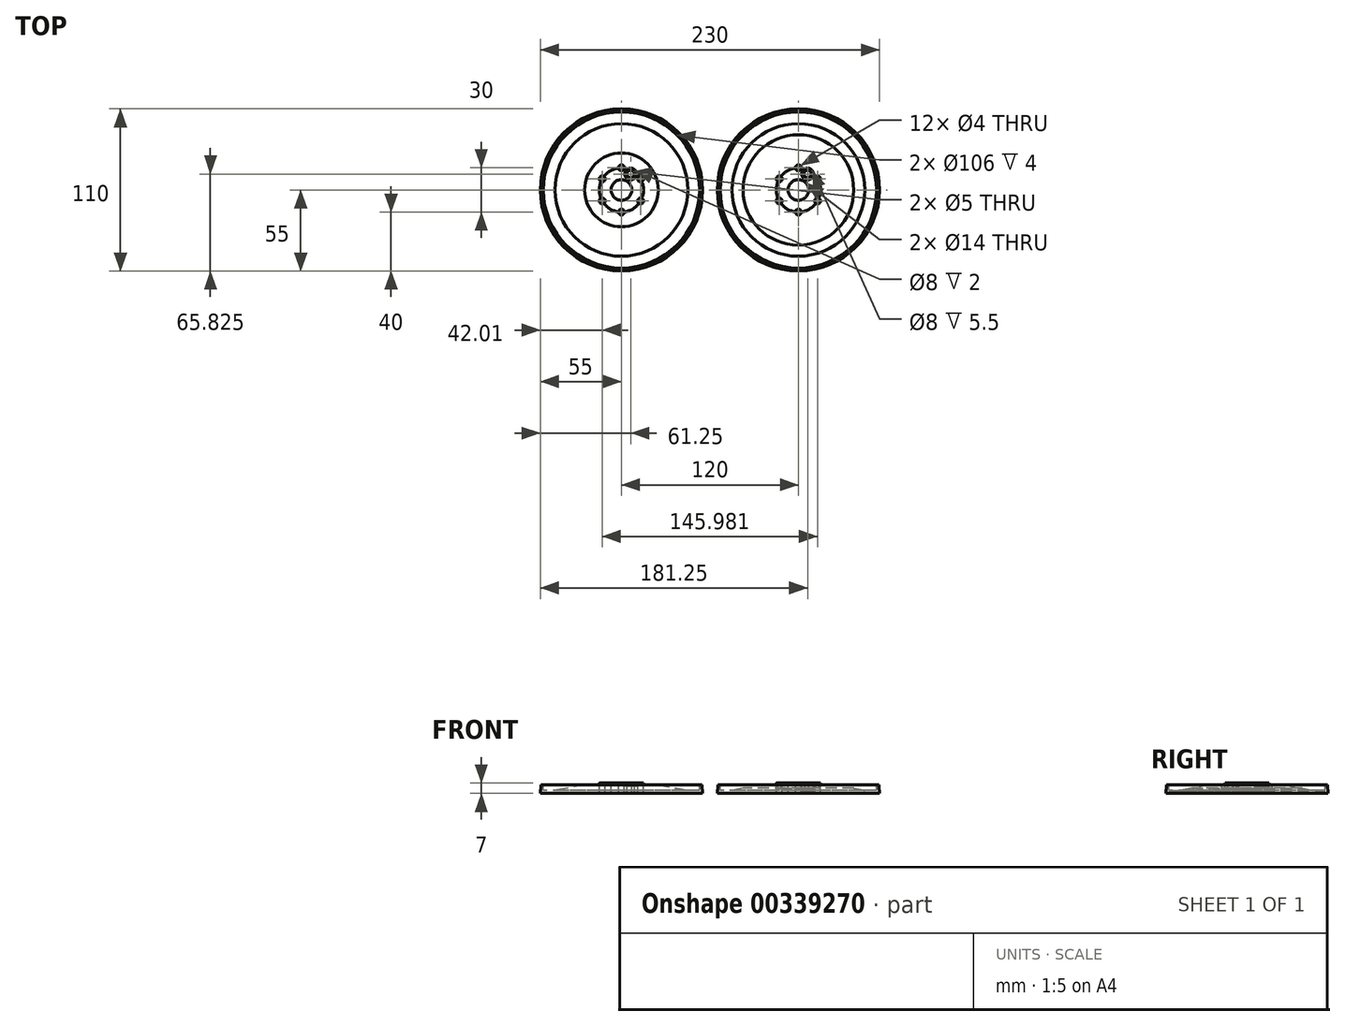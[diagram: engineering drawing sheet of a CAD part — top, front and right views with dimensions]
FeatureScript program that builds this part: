
annotation { "Feature Type Name" : "Feature", "Feature Type Description" : "" }
export const myFeature = defineFeature(function(context is Context, id is Id, definition is map)
    precondition{}
    {
        {
            var Q0;
            Q0=qCreatedBy(makeId("Front.planeOp"),FACE);
            var sketch = newSketch(context, id + "F0", { "sketchPlane" : qUnion([Q0])});
            skLineSegment(sketch, "E0", {"start": v(0, 0) * mm, "end": v(55, 0) * mm});
            skLineSegment(sketch, "E1", {"start": v(55, 0) * mm, "end": v(54.5, 6) * mm});
            skLineSegment(sketch, "E2", {"start": v(54.5, 6) * mm, "end": v(53, 6) * mm});
            skLineSegment(sketch, "E3", {"start": v(53, 6) * mm, "end": v(53, 2) * mm});
            skLineSegment(sketch, "E4", {"start": v(53, 2) * mm, "end": v(45, 2) * mm});
            skLineSegment(sketch, "E5", {"start": v(45, 2) * mm, "end": v(25, 6) * mm});
            skLineSegment(sketch, "E6", {"start": v(0, 7) * mm, "end": v(0, 0) * mm});
            skLineSegment(sketch, "E7", {"start": v(25, 6) * mm, "end": v(15, 6) * mm});
            skLineSegment(sketch, "E8", {"start": v(15, 6) * mm, "end": v(15, 7) * mm});
            skLineSegment(sketch, "E9", {"start": v(15, 7) * mm, "end": v(0, 7) * mm});
            skLineSegment(sketch, "E10", {"start": v(0, 25) * mm, "end": v(0, -25) * mm, "construction": true});
            skSolve(sketch);
        }
        {
            var Q0;
            Q0=makeQuery(id+"F0.imprint","IMPRINT",FACE,{"disambiguationData":[TD([[makeQuery(id+"F0.imprint","IMPRINT",EDGE,{"derivedFrom":sQuery(id+"F0.wireOp",EDGE,"E0")}),1.0]])]});
            var Q1;
            Q1=sQuery(id+"F0.wireOp",EDGE,"E10");
            revolve(context, id + "F1", {"entities" : qUnion([Q0]), "axis" : qUnion([Q1]), "revolveType" : RevolveType.FULL});
        }
        {
            var Q0;
            Q0=makeQuery(id+"F1.opRevolve","SWEPT_FACE",FACE,{"disambiguationData":[OSD([sQuery(id+"F0.wireOp",EDGE,"E9")])]});
            var sketch = newSketch(context, id + "F2", { "sketchPlane" : qUnion([Q0])});
            skCircle(sketch, "E11", {"center": v(0, 15) * mm, "radius": 2 * mm});
            skCircle(sketch, "E12", {"center": v(6.25, 10.83) * mm, "radius": 2.5 * mm});
            skCircle(sketch, "E13", {"center": v(6.25, 10.83) * mm, "radius": 4 * mm});
            skLineSegment(sketch, "E14", {"start": v(0, 15) * mm, "end": v(0, 0) * mm, "construction": true});
            skLineSegment(sketch, "E15", {"start": v(0, 0) * mm, "end": v(6.25, 10.83) * mm, "construction": true});
            skCircle(sketch, "E16.1.0", {"center": v(-13, 7.5) * mm, "radius": 2 * mm});
            skCircle(sketch, "E16.2.0", {"center": v(-13, -7.5) * mm, "radius": 2 * mm});
            skCircle(sketch, "E16.3.0", {"center": v(0, -15) * mm, "radius": 2 * mm});
            skCircle(sketch, "E16.4.0", {"center": v(13, -7.5) * mm, "radius": 2 * mm});
            skCircle(sketch, "E16.5.0", {"center": v(13, 7.5) * mm, "radius": 2 * mm});
            skPoint(sketch, "E16.center", {"position": v(0, 0) * mm});
            skLineSegment(sketch, "E17", {"start": v(13, 7.5) * mm, "end": v(0, 0) * mm, "construction": true});
            skLineSegment(sketch, "E18", {"start": v(0, 14.43) * mm, "end": v(12.5, 7.22) * mm, "construction": true});
            skLineSegment(sketch, "E19", {"start": v(-13, 7.5) * mm, "end": v(0, 0) * mm, "construction": true});
            skLineSegment(sketch, "E20", {"start": v(-13, -7.5) * mm, "end": v(0, 0) * mm, "construction": true});
            skLineSegment(sketch, "E21", {"start": v(0, -15) * mm, "end": v(0, 0) * mm, "construction": true});
            skLineSegment(sketch, "E22", {"start": v(13, -7.5) * mm, "end": v(0, 0) * mm, "construction": true});
            skSolve(sketch);
        }
        {
            var Q0;
            Q0=sQuery(id+"F2.wireOp",VERTEX,"E13.center");
            var Q1;
            Q1=makeQuery(id+"F1.opRevolve","SWEPT_BODY",BODY,{"disambiguationData":[OSD([sQuery(id+"F0.wireOp",EDGE,"E0"),sQuery(id+"F0.wireOp",EDGE,"E1"),sQuery(id+"F0.wireOp",EDGE,"E2"),sQuery(id+"F0.wireOp",EDGE,"E3"),sQuery(id+"F0.wireOp",EDGE,"E4"),sQuery(id+"F0.wireOp",EDGE,"E5"),sQuery(id+"F0.wireOp",EDGE,"E6"),sQuery(id+"F0.wireOp",EDGE,"E7"),sQuery(id+"F0.wireOp",EDGE,"E8"),sQuery(id+"F0.wireOp",EDGE,"E9")])]});
            hole(context, id + "F3", {"style" : HoleStyle.C_BORE, "endStyle" : HoleEndStyle.THROUGH, "standardTappedOrClearance" : lookupTablePath({ "standard" : "ISO", "engagement" : "75%", "pitch" : "0.8 mm", "size" : "M5", "type" : "Gewinde" }), "standardBlindInLast" : lookupTablePath({ "standard" : "ISO", "engagement" : "75%", "pitch" : "0.8 mm", "size" : "M5", "type" : "Gewinde" }), "holeDiameter" : 5 * mm, "cBoreDiameter" : 8 * mm, "cBoreDepth" : 2 * mm, "showTappedDepth" : true, "isTappedThrough" : true, "tappedDepth" : 12 * mm, "tapClearance" : 3, "startFromSketch" : true, "locations" : qUnion([Q0]), "scope" : qUnion([Q1])});
        }
        {
            var Q0;
            Q0=sQuery(id+"F2.wireOp",VERTEX,"E14.start");
            var Q1;
            Q1=sQuery(id+"F2.wireOp",VERTEX,"E16.5.0.center");
            var Q2;
            Q2=sQuery(id+"F2.wireOp",VERTEX,"E16.4.0.center");
            var Q3;
            Q3=sQuery(id+"F2.wireOp",VERTEX,"E16.3.0.center");
            var Q4;
            Q4=sQuery(id+"F2.wireOp",VERTEX,"E16.2.0.center");
            var Q5;
            Q5=sQuery(id+"F2.wireOp",VERTEX,"E16.1.0.center");
            var Q6;
            Q6=makeQuery(id+"F1.opRevolve","SWEPT_BODY",BODY,{"disambiguationData":[OSD([sQuery(id+"F0.wireOp",EDGE,"E0"),sQuery(id+"F0.wireOp",EDGE,"E1"),sQuery(id+"F0.wireOp",EDGE,"E2"),sQuery(id+"F0.wireOp",EDGE,"E3"),sQuery(id+"F0.wireOp",EDGE,"E4"),sQuery(id+"F0.wireOp",EDGE,"E5"),sQuery(id+"F0.wireOp",EDGE,"E6"),sQuery(id+"F0.wireOp",EDGE,"E7"),sQuery(id+"F0.wireOp",EDGE,"E8"),sQuery(id+"F0.wireOp",EDGE,"E9")])]});
            hole(context, id + "F4", {"style" : HoleStyle.SIMPLE, "endStyle" : HoleEndStyle.THROUGH, "standardTappedOrClearance" : lookupTablePath({ "standard" : "ISO", "size" : "4", "type" : "Gebohrt" }), "standardBlindInLast" : lookupTablePath({ "standard" : "ISO", "size" : "4", "type" : "Gebohrt" }), "holeDiameter" : 4 * mm, "isTappedThrough" : true, "tappedDepth" : 12 * mm, "tapClearance" : 3, "locations" : qUnion([Q0, Q1, Q2, Q3, Q4, Q5]), "scope" : qUnion([Q6])});
        }
        {
            var Q0;
            Q0=sQuery(id+"F2.wireOp",VERTEX,"E16.center");
            var Q1;
            Q1=makeQuery(id+"F1.opRevolve","SWEPT_BODY",BODY,{"disambiguationData":[OSD([sQuery(id+"F0.wireOp",EDGE,"E0"),sQuery(id+"F0.wireOp",EDGE,"E1"),sQuery(id+"F0.wireOp",EDGE,"E2"),sQuery(id+"F0.wireOp",EDGE,"E3"),sQuery(id+"F0.wireOp",EDGE,"E4"),sQuery(id+"F0.wireOp",EDGE,"E5"),sQuery(id+"F0.wireOp",EDGE,"E6"),sQuery(id+"F0.wireOp",EDGE,"E7"),sQuery(id+"F0.wireOp",EDGE,"E8"),sQuery(id+"F0.wireOp",EDGE,"E9")])]});
            hole(context, id + "F5", {"style" : HoleStyle.SIMPLE, "endStyle" : HoleEndStyle.THROUGH, "standardTappedOrClearance" : lookupTablePath({ "standard" : "ISO", "size" : "14", "type" : "Gebohrt" }), "standardBlindInLast" : lookupTablePath({ "standard" : "ISO", "size" : "14", "type" : "Gebohrt" }), "holeDiameter" : 14 * mm, "isTappedThrough" : true, "tappedDepth" : 12 * mm, "tapClearance" : 3, "locations" : qUnion([Q0]), "scope" : qUnion([Q1])});
        }
        {
            var Q0;
            Q0=makeQuery(id+"F1.opRevolve","SWEPT_BODY",BODY,{"disambiguationData":[OSD([sQuery(id+"F0.wireOp",EDGE,"E0"),sQuery(id+"F0.wireOp",EDGE,"E1"),sQuery(id+"F0.wireOp",EDGE,"E2"),sQuery(id+"F0.wireOp",EDGE,"E3"),sQuery(id+"F0.wireOp",EDGE,"E4"),sQuery(id+"F0.wireOp",EDGE,"E5"),sQuery(id+"F0.wireOp",EDGE,"E6"),sQuery(id+"F0.wireOp",EDGE,"E7"),sQuery(id+"F0.wireOp",EDGE,"E8"),sQuery(id+"F0.wireOp",EDGE,"E9")])]});
            transform(context, id + "F6", {"entities" : qUnion([Q0]), "transformType" : TransformType.TRANSLATION_3D, "dx" : 120 * mm, "dy" : 0 * mm, "dz" : 0 * mm, "makeCopy" : true});
        }
        {
            var Q0;
            Q0=makeQuery(id+"F6.opPattern","COPY",FACE,{"derivedFrom":makeQuery(id+"FyS3Qqui4xaS09H_1.boolean.opBoolean","SPLIT",FACE,{"disambiguationData":[TD([makeQuery(id+"F1.opRevolve","SWEPT_FACE",FACE,{"disambiguationData":[OSD([sQuery(id+"F0.wireOp",EDGE,"E6")])]})])],"derivedFrom":makeQuery(id+"F1.opRevolve","SWEPT_FACE",FACE,{"disambiguationData":[OSD([sQuery(id+"F0.wireOp",EDGE,"E9")])]})}),"instanceName":"1"});
            var sketch = newSketch(context, id + "F7", { "sketchPlane" : qUnion([Q0])});
            skCircle(sketch, "E23", {"center": v(120, 0) * mm, "radius": 50 * mm});
            skCircle(sketch, "E24.0", {"center": v(126.25, 10.83) * mm, "radius": 2.5 * mm});
            skSolve(sketch);
        }
        {
            var Q0;
            Q0=makeQuery(id+"F7.imprint","IMPRINT",FACE,{"disambiguationData":[TD([[makeQuery(id+"F7.imprint","IMPRINT",EDGE,{"derivedFrom":sQuery(id+"F7.wireOp",EDGE,"E23")}),1.0]])]});
            var Q1;
            {var subQ4=sQuery(id+"F2.wireOp",EDGE,"E11");var subQ11=makeQuery(id+"Fwcus1FpO5nh3Wj_1.opExtrude","CAP_EDGE",EDGE,{"disambiguationData":[OSD([subQ4])],"isStart":true});Q1=makeQuery(id+"F7.imprint","IMPRINT",FACE,{"disambiguationData":[TD([[makeQuery(id+"F7.imprint","IMPRINT",EDGE,{"derivedFrom":makeQuery(id+"F6.opPattern","COPY",EDGE,{"derivedFrom":makeQuery(id+"FkyFLQoTMtYrDj4_2.boolean.opBoolean","COPY",EDGE,{"derivedFrom":subQ11}),"instanceName":"1"})}),-1.0]])]});}
            var Q2;
            {var subQ17=sQuery(id+"F3.hole-0.sketch.wireOp",EDGE,"cbore_start_line_2");Q2=makeQuery(id+"F7.imprint","IMPRINT",FACE,{"disambiguationData":[TD([[makeQuery(id+"F7.imprint","IMPRINT",EDGE,{"derivedFrom":makeQuery(id+"F6.opPattern","COPY",EDGE,{"derivedFrom":makeQuery(id+"F3.hole-0.boolean.opBoolean","COPY",EDGE,{"derivedFrom":makeQuery(id+"F3.hole-0.opRevolve","SWEPT_EDGE",EDGE,{"disambiguationData":[OSD([subQ17,sQuery(id+"F3.hole-0.sketch.wireOp",EDGE,"cbore_start_line_3")])]})}),"instanceName":"1"})}),-1.0]])]});}
            extrude(context, id + "F8", {"entities" : qUnion([Q0, Q1, Q2]), "operationType" : NewBodyOperationType.REMOVE, "oppositeDirection" : true, "depth" : 3.5 * mm});
        }
        {
            var Q0;
            Q0=sQuery(id+"F7.wireOp",VERTEX,"E24.0.center");
            var Q1;
            Q1=makeQuery(id+"F6.opPattern","COPY",BODY,{"derivedFrom":makeQuery(id+"F1.opRevolve","SWEPT_BODY",BODY,{"disambiguationData":[OSD([sQuery(id+"F0.wireOp",EDGE,"E0"),sQuery(id+"F0.wireOp",EDGE,"E1"),sQuery(id+"F0.wireOp",EDGE,"E2"),sQuery(id+"F0.wireOp",EDGE,"E3"),sQuery(id+"F0.wireOp",EDGE,"E4"),sQuery(id+"F0.wireOp",EDGE,"E5"),sQuery(id+"F0.wireOp",EDGE,"E6"),sQuery(id+"F0.wireOp",EDGE,"E7"),sQuery(id+"F0.wireOp",EDGE,"E8"),sQuery(id+"F0.wireOp",EDGE,"E9")])]}),"instanceName":"1"});
            hole(context, id + "F9", {"style" : HoleStyle.C_BORE, "endStyle" : HoleEndStyle.THROUGH, "standardTappedOrClearance" : lookupTablePath({ "standard" : "ISO", "engagement" : "75%", "pitch" : "0.8 mm", "size" : "M5", "type" : "Gewinde" }), "standardBlindInLast" : lookupTablePath({ "standard" : "ISO", "engagement" : "75%", "pitch" : "0.8 mm", "size" : "M5", "type" : "Gewinde" }), "holeDiameter" : 5 * mm, "cBoreDiameter" : 8 * mm, "cBoreDepth" : 2 * mm, "showTappedDepth" : true, "isTappedThrough" : true, "tappedDepth" : 12 * mm, "tapClearance" : 3, "locations" : qUnion([Q0]), "scope" : qUnion([Q1])});
        }
    });
